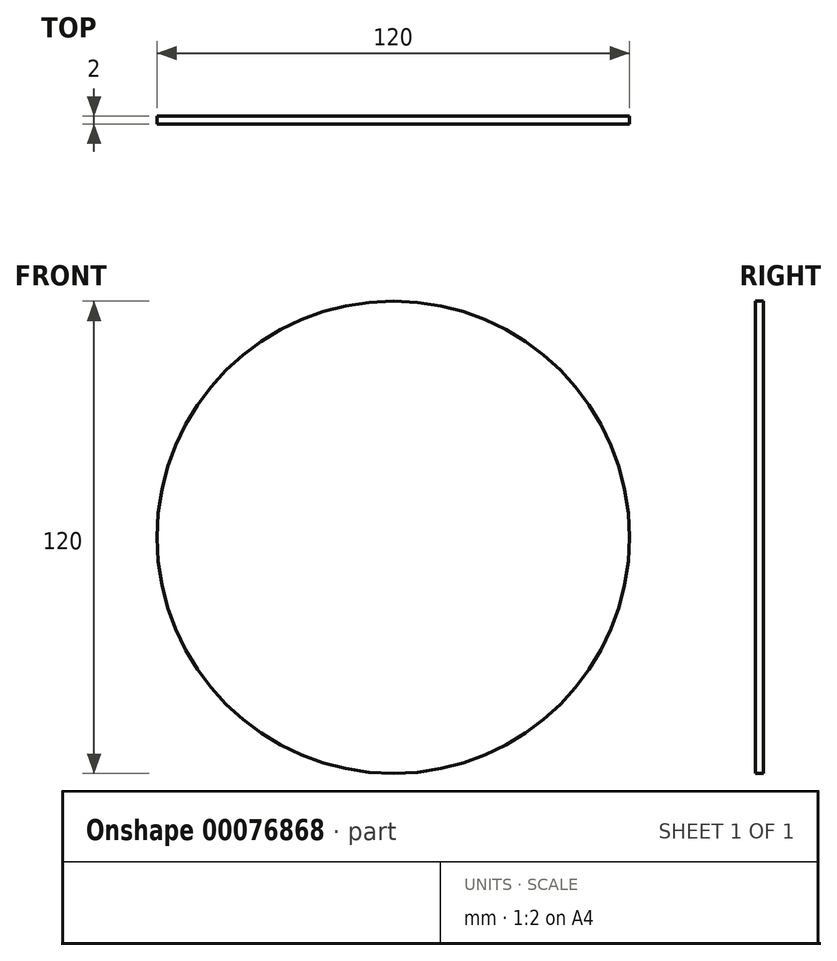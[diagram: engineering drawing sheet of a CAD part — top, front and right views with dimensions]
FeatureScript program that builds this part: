
annotation { "Feature Type Name" : "Feature", "Feature Type Description" : "" }
export const myFeature = defineFeature(function(context is Context, id is Id, definition is map)
    precondition{}
    {
        {
            var Q0;
            Q0=qCreatedBy(makeId("Front.planeOp"),FACE);
            var sketch = newSketch(context, id + "F0", { "sketchPlane" : qUnion([Q0])});
            skCircle(sketch, "E0", {"center": v(0, 0) * mm, "radius": 60 * mm});
            skSolve(sketch);
        }
        {
            var Q0;
            Q0=makeQuery(id+"F0.imprint","IMPRINT",FACE,{"disambiguationData":[TD([[makeQuery(id+"F0.imprint","IMPRINT",EDGE,{"derivedFrom":sQuery(id+"F0.wireOp",EDGE,"E0")}),1.0]])]});
            extrude(context, id + "F1", {"entities" : qUnion([Q0]), "depth" : 2 * mm});
        }
    });
